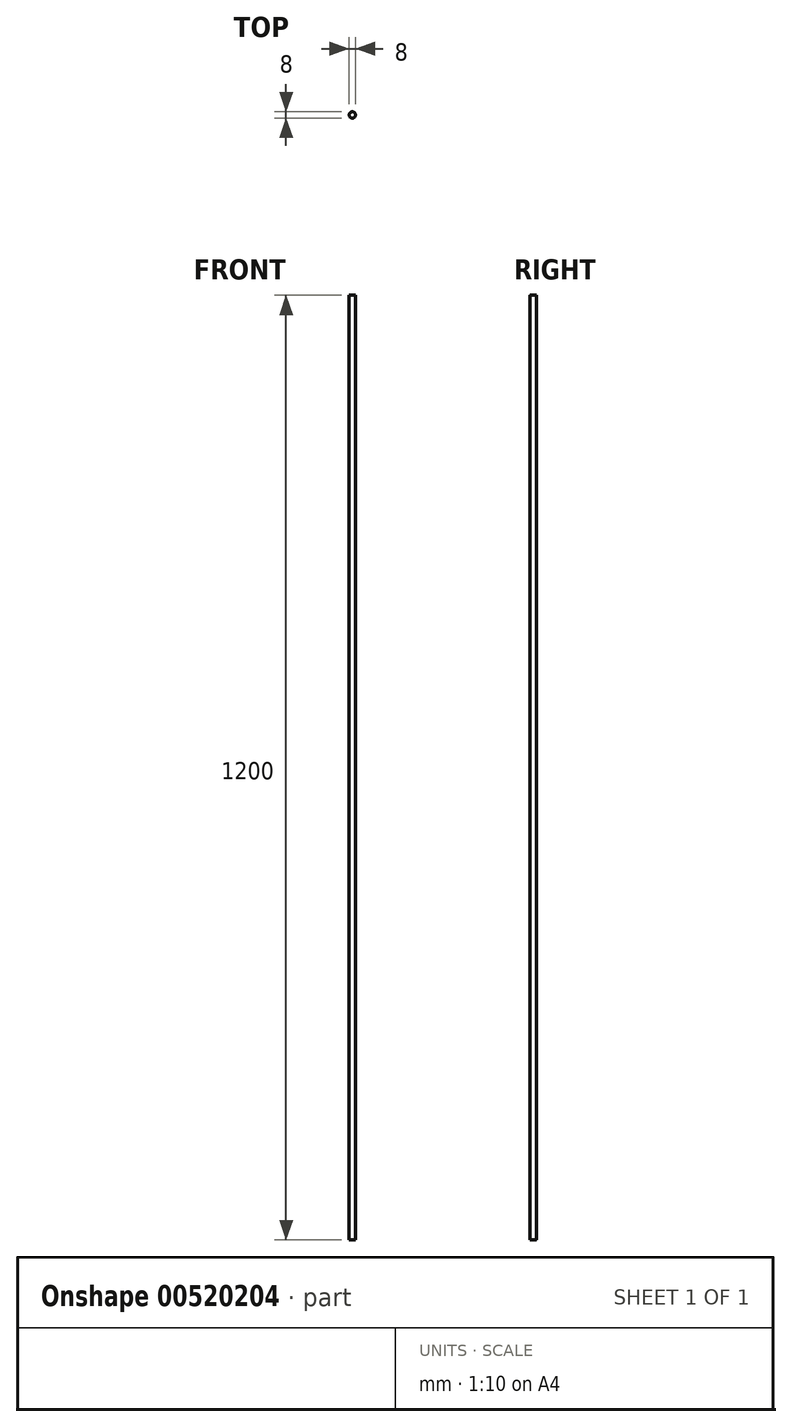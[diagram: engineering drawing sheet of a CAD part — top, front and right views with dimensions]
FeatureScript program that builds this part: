
annotation { "Feature Type Name" : "Feature", "Feature Type Description" : "" }
export const myFeature = defineFeature(function(context is Context, id is Id, definition is map)
    precondition{}
    {
        {
            var Q0;
            Q0=qCreatedBy(makeId("Top.planeOp"),FACE);
            var sketch = newSketch(context, id + "F0", { "sketchPlane" : qUnion([Q0])});
            skCircle(sketch, "E0", {"center": v(0, 0) * mm, "radius": 4 * mm});
            skSolve(sketch);
        }
        {
            var Q0;
            Q0 = qSketchRegion(id + "F0", true);
            extrude(context, id + "F1", {"entities" : qUnion([Q0]), "depth" : 1200 * mm, "offsetDistance" : 25 * mm});
        }
    });
